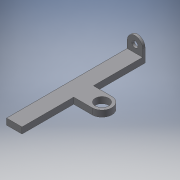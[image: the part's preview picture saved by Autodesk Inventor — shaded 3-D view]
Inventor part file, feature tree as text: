
AUTODESK INVENTOR PART (.ipt)
format: ipt  version: 2017 (Build 210142000, 142)  size: 173,056 bytes
history: native  units: mm
features: extrude x7, sketch x7, other x3, reference x1
ambient origin geometry x8: Origin, YZ Plane, XZ Plane, XY Plane, X Axis, Y Axis, Z Axis, Center Point
bodies: Solid1 (feature_tree)
feature tree (18):
  extrude  "Extrusion1"  Depth=5.0mm
  extrude  "Extrusion2"  Depth=30.0mm
  extrude  "Extrusion3"  Depth=10.0mm TaperAngle=0.0deg
  extrude  "Extrusion4"  Depth=10.0mm
  extrude  "Extrusion5"  Depth=4.0mm
  extrude  "Extrusion6"  Depth=5.1mm TaperAngle=0.0deg
  extrude  "Extrusion7"  Depth=6.0mm
  sketch  "Sketch1"  dims[d0=22.0mm d1=5.0mm]
  sketch  "Sketch2"  dims[d2=30.0mm d3=260.0mm]
  sketch  "Sketch3"  dims[d4=25.0mm d5=10.0mm d6=0.0mm]
  sketch  "Sketch4"  dims[d7=10.0mm d8=12.0mm]
  sketch  "Sketch5"  dims[d9=4.0mm d10=0.0mm d11=100.0mm]
  reference  "Reference2"
  sketch  "Sketch6"  dims[d12=10.0mm d13=0.0mm d14=5.1mm d15=0.0mm]
  sketch  "Sketch7"  dims[d16=10.0mm d17=0.0mm d18=6.0mm d19=10.0mm d20=0.0mm d21=5.0mm d22=20.0mm d23=35.0mm d24=80.0mm d25=10.0mm d26=0.0mm]
  other  "Assembly2.iam"
  other  "CJ2B16-100Z:1"
  other  "CJ2B16-100Z_5:1"
